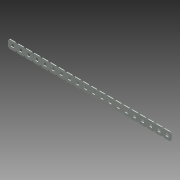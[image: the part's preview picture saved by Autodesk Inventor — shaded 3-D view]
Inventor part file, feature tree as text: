
AUTODESK INVENTOR PART (.ipt)
format: ipt  version: 2013 (Build 170138000, 138)  size: 378,368 bytes
history: native  units: mm (DEFAULTED — no unit token found)
features: other x21, extrude x20, pattern_linear x2, sketch x2, sheet_metal_op x1
ambient origin geometry x8: Origin, YZ Plane, XZ Plane, XY Plane, X Axis, Y Axis, Z Axis, Center Point
bodies: Solid1 (feature_tree)
feature tree (46):
  sheet_metal_op  "Face1"
  pattern_linear  "Rectangular Pattern1"  Spacing1=1.905mm  [1 undecoded]
  pattern_linear  "Rectangular Pattern2"  Spacing1=1.905mm  [1 undecoded]
  sketch  "Sketch1"  dims[d0=12.7mm]
  other  "Plate1"
  sketch  "Sketch4"  dims[d1=12.7mm d2=1.905mm d3=1.905mm d4=1.905mm d5=1.905mm d6=1.905mm d7=1.905mm d8=1.905mm d9=1.905mm d10=4.6228mm d11=4.6228mm d12=4.064mm d13=4.064mm d14=1.27mm d15=200.0mm d17=12.7mm d18=0.508mm d19=25.4mm d20=0.0mm d21=200.0mm d23=12.7mm d24=0.0mm d25=0.0mm d26=0.0mm d27=0.0mm d28=0.0mm d29=0.0mm d30=0.0mm d31=0.0mm d32=0.0mm d33=0.0mm d34=0.0mm d35=0.0mm d36=0.0mm d37=0.0mm d38=0.0mm d39=0.0mm d40=0.0mm d41=0.0mm d42=0.0mm d43=0.0mm d44=0.0mm d45=0.0mm d46=0.0mm d47=0.0mm d48=0.0mm d49=0.0mm d50=0.0mm d51=0.0mm d52=0.0mm d53=0.0mm d54=0.0mm d55=0.0mm d56=0.0mm d57=0.0mm d58=0.0mm d59=0.0mm d60=0.0mm d61=0.0mm d62=0.0mm d63=0.0mm]
  other  "Srf1"
  other  "Srf2"
  other  "Srf3"
  other  "Srf4"
  other  "Srf5"
  other  "Srf6"
  other  "Srf7"
  other  "Srf8"
  other  "Srf9"
  other  "Srf10"
  other  "Srf11"
  other  "Srf12"
  other  "Srf13"
  other  "Srf14"
  other  "Srf15"
  other  "Srf16"
  other  "Srf17"
  other  "Srf18"
  other  "Srf19"
  other  "Srf20"
  extrude  "ExtrusionSrf1"  Depth=1.905mm
  extrude  "ExtrusionSrf2"  Depth=1.905mm
  extrude  "ExtrusionSrf3"  Depth=1.905mm
  extrude  "ExtrusionSrf4"  Depth=1.905mm
  extrude  "ExtrusionSrf5"  Depth=1.905mm
  extrude  "ExtrusionSrf6"  Depth=1.905mm
  extrude  "ExtrusionSrf7"  Depth=4.6228mm
  extrude  "ExtrusionSrf8"  Depth=4.6228mm
  extrude  "ExtrusionSrf9"  Depth=4.064mm
  extrude  "ExtrusionSrf10"  Depth=4.064mm
  extrude  "ExtrusionSrf11"  Depth=1.27mm
  extrude  "ExtrusionSrf12"  Depth=200.0mm
  extrude  "ExtrusionSrf13"  Depth=0.508mm
  extrude  "ExtrusionSrf14"  Depth=25.4mm TaperAngle=0.0deg
  extrude  "ExtrusionSrf15"  Depth=200.0mm
  extrude  "ExtrusionSrf16"  [1 undecoded]
  extrude  "ExtrusionSrf17"  [1 undecoded]
  extrude  "ExtrusionSrf18"  [1 undecoded]
  extrude  "ExtrusionSrf19"  [1 undecoded]
  extrude  "ExtrusionSrf20"  [1 undecoded]
note: 7 required parameter values undecoded (feature->parameter linkage not recoverable at this tier; creation-order binding heuristic only, values carry confidence <= 0.55)
